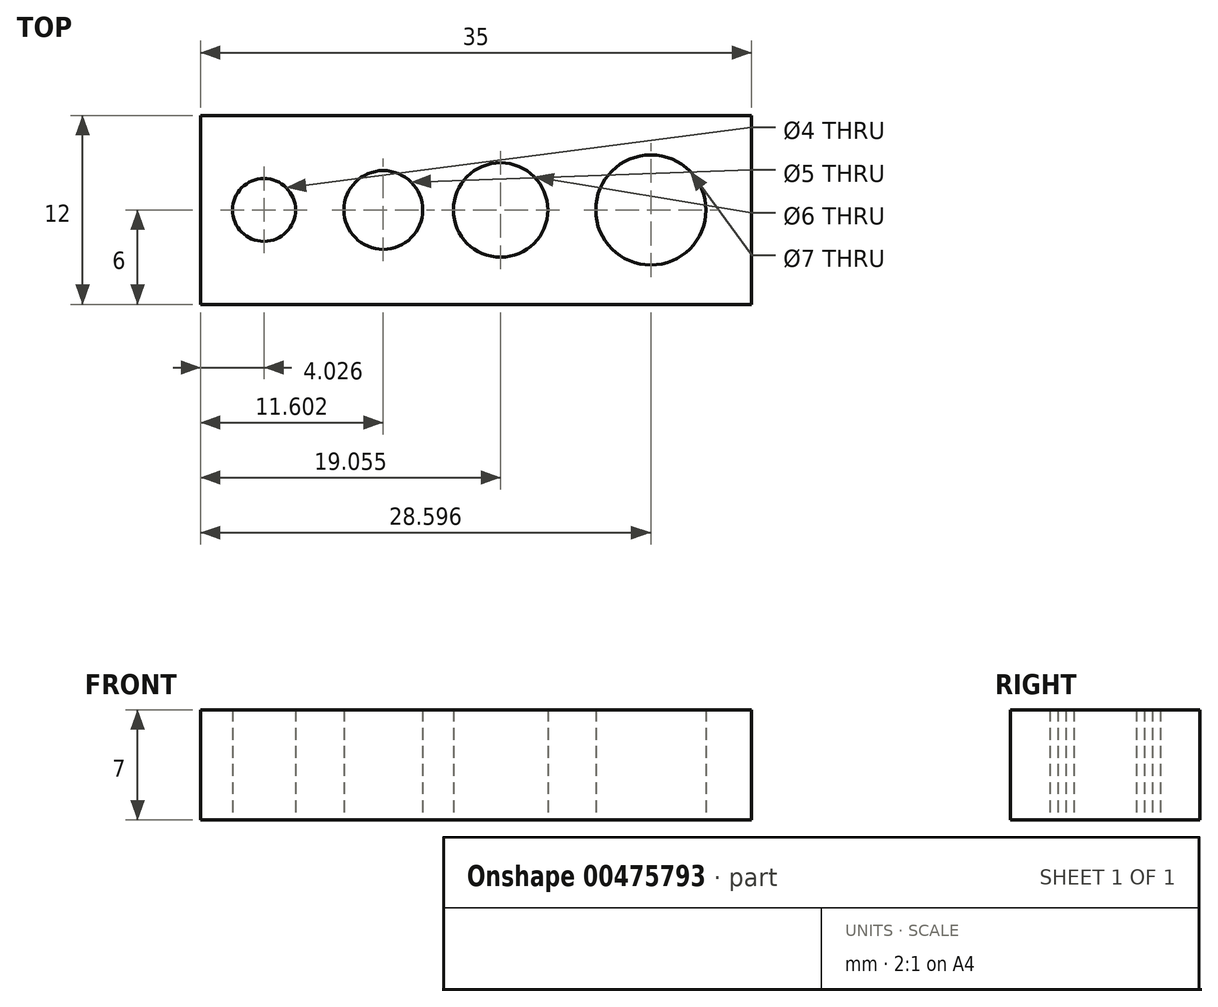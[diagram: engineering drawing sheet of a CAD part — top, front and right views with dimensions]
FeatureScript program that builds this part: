
annotation { "Feature Type Name" : "Feature", "Feature Type Description" : "" }
export const myFeature = defineFeature(function(context is Context, id is Id, definition is map)
    precondition{}
    {
        {
            var Q0;
            Q0=qCreatedBy(makeId("Top.planeOp"),FACE);
            var sketch = newSketch(context, id + "F0", { "sketchPlane" : qUnion([Q0])});
            skLineSegment(sketch, "E0.bottom", {"start": v(-31.12, 11.9) * mm, "end": v(3.88, 11.9) * mm});
            skLineSegment(sketch, "E0.top", {"start": v(-31.12, -0.1) * mm, "end": v(3.88, -0.1) * mm});
            skLineSegment(sketch, "E0.left", {"start": v(-31.12, 11.9) * mm, "end": v(-31.12, -0.1) * mm});
            skLineSegment(sketch, "E0.right", {"start": v(3.88, 11.9) * mm, "end": v(3.88, -0.1) * mm});
            skLineSegment(sketch, "E1", {"start": v(-31.12, 5.9) * mm, "end": v(3.88, 5.9) * mm, "construction": true});
            skCircle(sketch, "E2", {"center": v(-27.1, 5.9) * mm, "radius": 2 * mm});
            skCircle(sketch, "E3", {"center": v(-19.52, 5.9) * mm, "radius": 2.5 * mm});
            skCircle(sketch, "E4", {"center": v(-12.06, 5.9) * mm, "radius": 3 * mm});
            skCircle(sketch, "E5", {"center": v(-2.52, 5.9) * mm, "radius": 3.5 * mm});
            skSolve(sketch);
        }
        {
            var Q0;
            Q0 = qSketchRegion(id + "F0", true);
            extrude(context, id + "F1", {"entities" : qUnion([Q0]), "depth" : 7 * mm});
        }
    });
